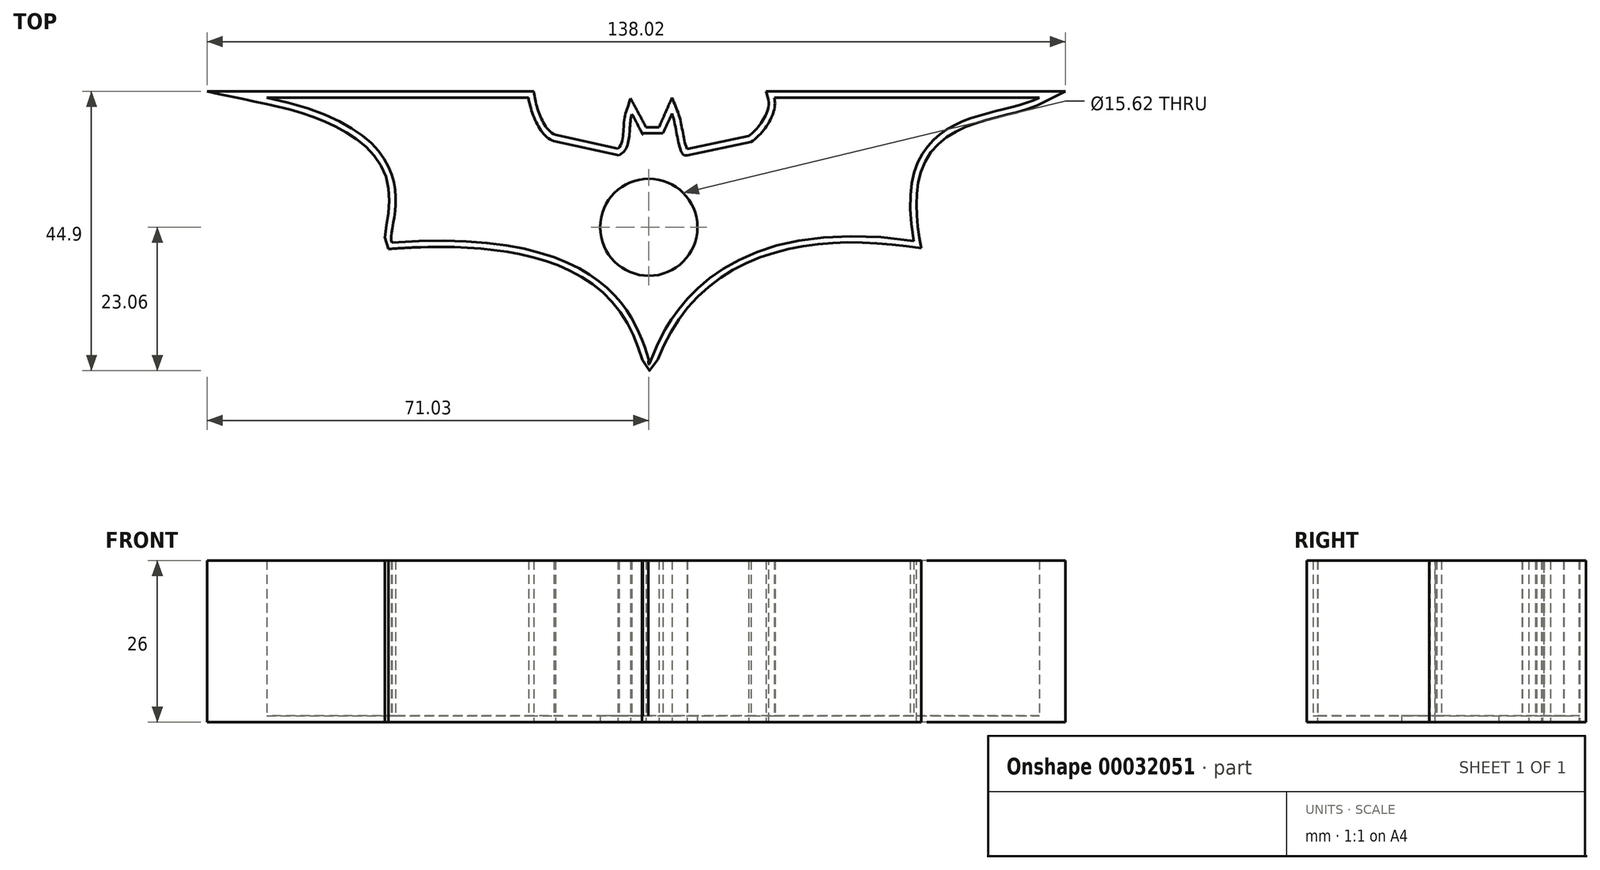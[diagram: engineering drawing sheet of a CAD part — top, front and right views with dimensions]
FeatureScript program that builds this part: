
annotation { "Feature Type Name" : "Feature", "Feature Type Description" : "" }
export const myFeature = defineFeature(function(context is Context, id is Id, definition is map)
    precondition{}
    {
        {
            var Q0;
            Q0=qCreatedBy(makeId("Top.planeOp"),FACE);
            var sketch = newSketch(context, id + "F0", { "sketchPlane" : qUnion([Q0])});
            skLineSegment(sketch, "E0", {"start": v(-61.42, 20.84) * mm, "end": v(-19.36, 20.84) * mm});
            skLineSegment(sketch, "E1", {"start": v(20.16, 20.84) * mm, "end": v(62.8, 20.84) * mm});
            skLineSegment(sketch, "E2", {"start": v(6.2, 11.6) * mm, "end": v(16.46, 13.7) * mm});
            skLineSegment(sketch, "E3", {"start": v(-15.29, 13.87) * mm, "end": v(-4.78, 11.57) * mm});
            skFitSpline(sketch, "E4", {"points": [v(-19.36, 20.84) * mm, v(-15.29, 13.87) * mm], "startDerivative": vector(1.15, -7.06) * mm, "endDerivative": vector(6.84, -2.07) * mm});
            skFitSpline(sketch, "E5", {"points": [v(16.46, 13.7) * mm, v(20.16, 20.84) * mm], "startDerivative": vector(7.2, 5.17) * mm, "endDerivative": vector(-1.84, 6.58) * mm});
            skFitSpline(sketch, "E6", {"points": [v(62.8, 20.84) * mm, v(42.58, -2.2) * mm], "startDerivative": vector(-21.57, -10.9) * mm, "endDerivative": vector(11.61, -65.03) * mm});
            skFitSpline(sketch, "E7", {"points": [v(42.58, -2.2) * mm, v(0, -22.06) * mm, v(0, -21.29) * mm], "startDerivative": vector(-126.66, 18.34) * mm, "endDerivative": vector(2.73, 8.47) * mm});
            skFitSpline(sketch, "E8", {"points": [v(0, -21.29) * mm, v(-41.29, -2.45) * mm], "startDerivative": vector(-6.97, 22.45) * mm, "endDerivative": vector(-102.19, -7.35) * mm});
            skFitSpline(sketch, "E9", {"points": [v(-41.29, -2.45) * mm, v(-61.42, 20.84) * mm], "startDerivative": vector(-3.87, 7.35) * mm, "endDerivative": vector(-85.4, 17.95) * mm});
            skFitSpline(sketch, "E10", {"points": [v(-4.78, 11.57) * mm, v(-2.72, 18.19) * mm], "startDerivative": vector(6.74, 3.4) * mm, "endDerivative": vector(2.1, 6.27) * mm});
            skFitSpline(sketch, "E11", {"points": [v(-2.72, 18.19) * mm, v(-1.03, 14.98) * mm, v(-1, 14.92) * mm, v(-0.95, 15.1) * mm], "startDerivative": vector(3, -5.6) * mm, "endDerivative": vector(0.65, -0.26) * mm});
            skFitSpline(sketch, "E12", {"points": [v(2.3, 15.1) * mm, v(3.7, 18.27) * mm], "startDerivative": vector(1.47, 3.38) * mm, "endDerivative": vector(1.47, 3.38) * mm});
            skFitSpline(sketch, "E13", {"points": [v(3.7, 18.27) * mm, v(6.2, 11.6) * mm], "startDerivative": vector(2.66, -6.43) * mm, "endDerivative": vector(4.53, 2.2) * mm});
            skFitSpline(sketch, "E14", {"points": [v(-0.95, 15.1) * mm, v(2.3, 15.1) * mm], "startDerivative": vector(3.24, 0) * mm, "endDerivative": vector(3.24, 0) * mm});
            skSolve(sketch);
        }
        {
            var Q0;
            Q0=makeQuery(id+"F0.imprint","IMPRINT",FACE,{"disambiguationData":[TD([[makeQuery(id+"F0.imprint","IMPRINT",EDGE,{"derivedFrom":sQuery(id+"F0.wireOp",EDGE,"E0")}),-1.0]])]});
            extrude(context, id + "F1", {"entities" : qUnion([Q0]), "depth" : 25 * mm});
        }
        {
            var Q0;
            Q0=makeQuery(id+"F1.opExtrude","CAP_FACE",FACE,{"disambiguationData":[OSD([sQuery(id+"F0.wireOp",EDGE,"E0"),sQuery(id+"F0.wireOp",EDGE,"E1"),sQuery(id+"F0.wireOp",EDGE,"E2"),sQuery(id+"F0.wireOp",EDGE,"E3"),sQuery(id+"F0.wireOp",EDGE,"E4"),sQuery(id+"F0.wireOp",EDGE,"E5"),sQuery(id+"F0.wireOp",EDGE,"E6"),sQuery(id+"F0.wireOp",EDGE,"E7"),sQuery(id+"F0.wireOp",EDGE,"E8"),sQuery(id+"F0.wireOp",EDGE,"E9"),sQuery(id+"F0.wireOp",EDGE,"E10"),sQuery(id+"F0.wireOp",EDGE,"E11"),sQuery(id+"F0.wireOp",EDGE,"E12"),sQuery(id+"F0.wireOp",EDGE,"E13"),sQuery(id+"F0.wireOp",EDGE,"E14")])],"isStart":false});
            shell(context, id + "F2", {"entities" : qUnion([Q0]), "thickness" : 1 * mm, "oppositeDirection" : true});
        }
        {
            var Q0;
            Q0=makeQuery(id+"F1.opExtrude","CAP_FACE",FACE,{"disambiguationData":[OSD([sQuery(id+"F0.wireOp",EDGE,"E0"),sQuery(id+"F0.wireOp",EDGE,"E1"),sQuery(id+"F0.wireOp",EDGE,"E2"),sQuery(id+"F0.wireOp",EDGE,"E3"),sQuery(id+"F0.wireOp",EDGE,"E4"),sQuery(id+"F0.wireOp",EDGE,"E5"),sQuery(id+"F0.wireOp",EDGE,"E6"),sQuery(id+"F0.wireOp",EDGE,"E7"),sQuery(id+"F0.wireOp",EDGE,"E8"),sQuery(id+"F0.wireOp",EDGE,"E9"),sQuery(id+"F0.wireOp",EDGE,"E10"),sQuery(id+"F0.wireOp",EDGE,"E11"),sQuery(id+"F0.wireOp",EDGE,"E12"),sQuery(id+"F0.wireOp",EDGE,"E13"),sQuery(id+"F0.wireOp",EDGE,"E14")])],"isStart":true});
            var sketch = newSketch(context, id + "F3", { "sketchPlane" : qUnion([Q0])});
            skCircle(sketch, "E15", {"center": v(0, 0) * mm, "radius": 7.8 * mm});
            skSolve(sketch);
        }
        {
            var Q0;
            Q0 = qSketchRegion(id + "F3", true);
            extrude(context, id + "F4", {"entities" : qUnion([Q0]), "operationType" : NewBodyOperationType.REMOVE, "oppositeDirection" : true, "depth" : 25.4 * mm});
        }
    });
